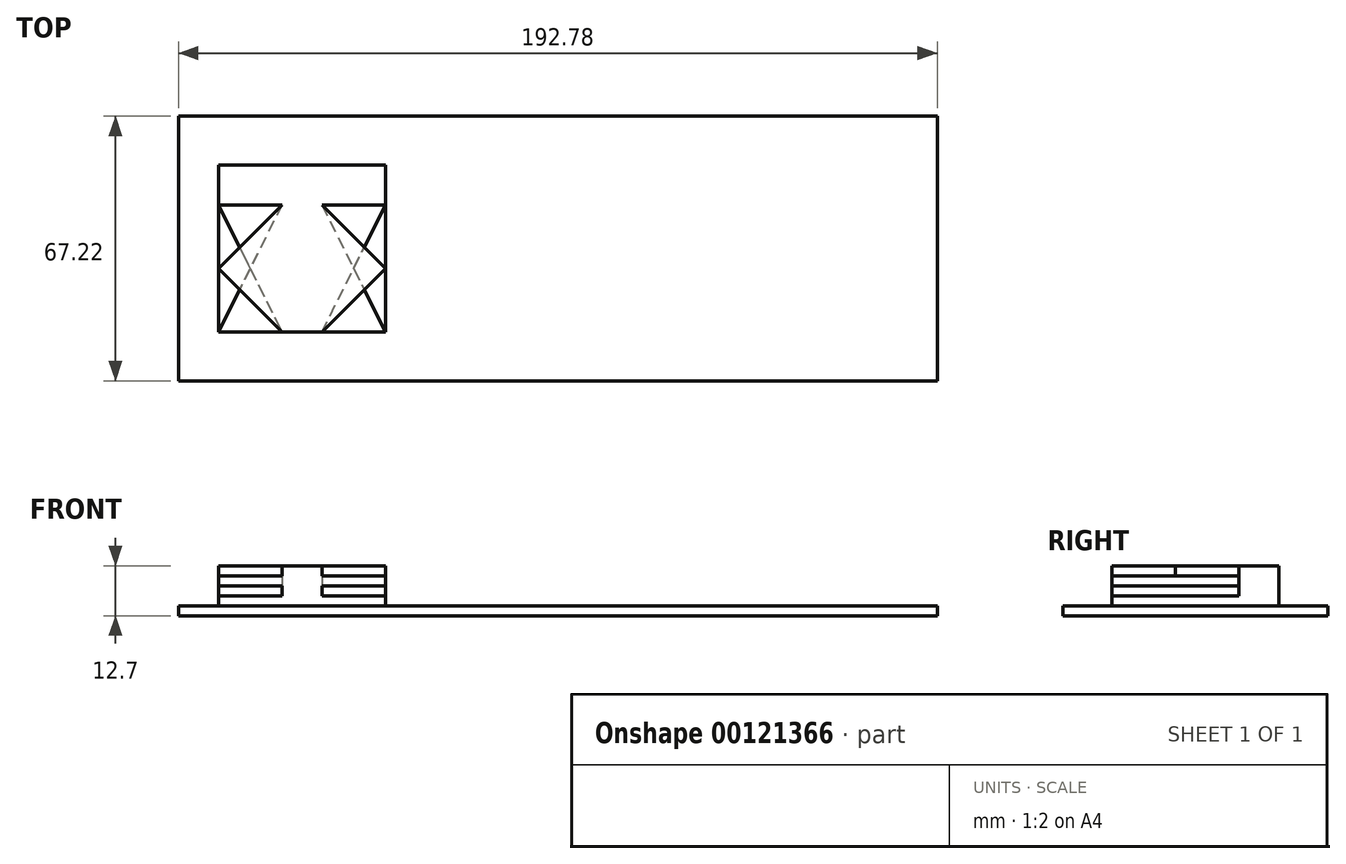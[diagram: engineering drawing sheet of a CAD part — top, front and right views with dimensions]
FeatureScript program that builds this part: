
annotation { "Feature Type Name" : "Feature", "Feature Type Description" : "" }
export const myFeature = defineFeature(function(context is Context, id is Id, definition is map)
    precondition{}
    {
        {
            var Q0;
            Q0=qCreatedBy(makeId("Top.planeOp"),FACE);
            var sketch = newSketch(context, id + "F0", { "sketchPlane" : qUnion([Q0])});
            skLineSegment(sketch, "E0", {"start": v(12479.9, 12174.65) * mm, "end": v(8845.28, 8523.8) * mm});
            skLineSegment(sketch, "E1", {"start": v(8845.28, 8523.8) * mm, "end": v(12479.9, 4895.02) * mm});
            skLineSegment(sketch, "E2", {"start": v(12479.9, 4895.02) * mm, "end": v(12479.9, 12174.65) * mm});
            skLineSegment(sketch, "E3", {"start": v(15099.98, 12172.42) * mm, "end": v(15099.98, 4895.02) * mm});
            skLineSegment(sketch, "E4", {"start": v(15099.98, 4895.02) * mm, "end": v(18732.48, 4895.02) * mm});
            skLineSegment(sketch, "E5", {"start": v(18732.48, 4895.02) * mm, "end": v(15099.98, 12172.42) * mm});
            skLineSegment(sketch, "E6", {"start": v(883.22, 12179.96) * mm, "end": v(4533.88, 12179.96) * mm});
            skLineSegment(sketch, "E7", {"start": v(4533.88, 12179.96) * mm, "end": v(4533.88, 14765.45) * mm});
            skLineSegment(sketch, "E8", {"start": v(4533.88, 14765.45) * mm, "end": v(-5353.25, 14765.45) * mm});
            skLineSegment(sketch, "E9", {"start": v(-5353.25, 14765.45) * mm, "end": v(-5353.25, 12179.96) * mm});
            skLineSegment(sketch, "E10", {"start": v(-5353.25, 12179.96) * mm, "end": v(-1702.6, 12179.96) * mm});
            skLineSegment(sketch, "E11", {"start": v(-1702.6, 12179.96) * mm, "end": v(-1702.6, 4879.79) * mm});
            skLineSegment(sketch, "E12", {"start": v(-1702.6, 4879.79) * mm, "end": v(883.22, 4879.79) * mm});
            skLineSegment(sketch, "E13", {"start": v(883.22, 4879.79) * mm, "end": v(883.22, 12179.96) * mm});
            skLineSegment(sketch, "E14", {"start": v(-18732.48, 14750.42) * mm, "end": v(-8865.64, 14750.42) * mm});
            skLineSegment(sketch, "E15", {"start": v(-8865.64, 14750.42) * mm, "end": v(-8865.64, 4894.82) * mm});
            skLineSegment(sketch, "E16", {"start": v(-8865.64, 4894.82) * mm, "end": v(-18732.48, 4894.82) * mm});
            skLineSegment(sketch, "E17", {"start": v(-18732.48, 4894.82) * mm, "end": v(-18732.48, 14750.42) * mm});
            skLineSegment(sketch, "E18.bottom", {"start": v(96.39, -33.61) * mm, "end": v(-96.39, -33.61) * mm});
            skLineSegment(sketch, "E18.top", {"start": v(96.39, 33.61) * mm, "end": v(-96.39, 33.61) * mm});
            skLineSegment(sketch, "E18.left", {"start": v(96.39, -33.61) * mm, "end": v(96.39, 33.61) * mm});
            skLineSegment(sketch, "E18.right", {"start": v(-96.39, -33.61) * mm, "end": v(-96.39, 33.61) * mm});
            skPoint(sketch, "E18.middle", {"position": v(0, 0) * mm});
            skSolve(sketch);
        }
        {
            var Q0;
            Q0=makeQuery(id+"F0.imprint","IMPRINT",FACE,{"disambiguationData":[TD([[makeQuery(id+"F0.imprint","IMPRINT",EDGE,{"derivedFrom":sQuery(id+"F0.wireOp",EDGE,"FW5R2YLv-ctxC-GVFr-Jofu-nXype2otcPYi.bottom")}),-1.0]])]});
            var Q1;
            Q1=makeQuery(id+"F0.imprint","IMPRINT",FACE,{"disambiguationData":[TD([[makeQuery(id+"F0.imprint","IMPRINT",EDGE,{"derivedFrom":sQuery(id+"F0.wireOp",EDGE,"E18.bottom")}),-1.0]])]});
            extrude(context, id + "F1", {"entities" : qUnion([Q0, Q1]), "depth" : 2.54 * mm});
        }
        {
            var Q0;
            Q0=makeQuery(id+"F1.opExtrude","CAP_FACE",FACE,{"disambiguationData":[OSD([sQuery(id+"F0.wireOp",EDGE,"E18.bottom"),sQuery(id+"F0.wireOp",EDGE,"E18.top"),sQuery(id+"F0.wireOp",EDGE,"E18.left"),sQuery(id+"F0.wireOp",EDGE,"E18.right")])],"isStart":false});
            var sketch = newSketch(context, id + "F2", { "sketchPlane" : qUnion([Q0])});
            skLineSegment(sketch, "E19.bottom", {"start": v(-43.8, -21.22) * mm, "end": v(-86.23, -21.22) * mm});
            skLineSegment(sketch, "E19.top", {"start": v(-43.8, 21.22) * mm, "end": v(-86.23, 21.22) * mm});
            skLineSegment(sketch, "E19.left", {"start": v(-43.8, -21.22) * mm, "end": v(-43.8, 21.22) * mm});
            skLineSegment(sketch, "E19.right", {"start": v(-86.23, -21.22) * mm, "end": v(-86.23, 21.22) * mm});
            skPoint(sketch, "E19.middle", {"position": v(-65.01, 0) * mm});
            skSolve(sketch);
        }
        {
            var Q0;
            Q0=makeQuery(id+"F2.imprint","IMPRINT",FACE,{"disambiguationData":[TD([[makeQuery(id+"F2.imprint","IMPRINT",EDGE,{"derivedFrom":sQuery(id+"F2.wireOp",EDGE,"E19.bottom")}),-1.0]])]});
            extrude(context, id + "F3", {"entities" : qUnion([Q0]), "depth" : 2.54 * mm});
        }
        {
            var Q0;
            Q0=makeQuery(id+"F3.opExtrude","CAP_FACE",FACE,{"disambiguationData":[OSD([sQuery(id+"F2.wireOp",EDGE,"E19.bottom"),sQuery(id+"F2.wireOp",EDGE,"E19.top"),sQuery(id+"F2.wireOp",EDGE,"E19.left"),sQuery(id+"F2.wireOp",EDGE,"E19.right")])],"isStart":false});
            var sketch = newSketch(context, id + "F4", { "sketchPlane" : qUnion([Q0])});
            skLineSegment(sketch, "E20", {"start": v(-86.23, 21.22) * mm, "end": v(-86.23, 11.06) * mm});
            skLineSegment(sketch, "E21", {"start": v(-86.23, 11.06) * mm, "end": v(-70.1, 11.06) * mm});
            skLineSegment(sketch, "E22", {"start": v(-70.1, 11.06) * mm, "end": v(-70.1, -21.22) * mm});
            skLineSegment(sketch, "E23", {"start": v(-70.1, -21.22) * mm, "end": v(-59.93, -21.22) * mm});
            skLineSegment(sketch, "E24", {"start": v(-59.93, -21.22) * mm, "end": v(-59.93, 11.06) * mm});
            skLineSegment(sketch, "E25", {"start": v(-59.93, 11.06) * mm, "end": v(-43.8, 11.06) * mm});
            skLineSegment(sketch, "E26", {"start": v(-43.8, 11.06) * mm, "end": v(-43.8, 21.22) * mm});
            skLineSegment(sketch, "E27", {"start": v(-43.8, 21.22) * mm, "end": v(-86.23, 21.22) * mm});
            skPoint(sketch, "E28", {"position": v(-65.01, -21.22) * mm});
            skSolve(sketch);
        }
        {
            var Q0;
            Q0=makeQuery(id+"F4.imprint","IMPRINT",FACE,{"disambiguationData":[TD([[makeQuery(id+"F4.imprint","IMPRINT",EDGE,{"derivedFrom":sQuery(id+"F4.wireOp",EDGE,"E20")}),-1.0]])]});
            extrude(context, id + "F5", {"entities" : qUnion([Q0]), "depth" : 7.62 * mm});
        }
        {
            var Q0;
            Q0=makeQuery(id+"F3.opExtrude","CAP_FACE",FACE,{"disambiguationData":[OSD([sQuery(id+"F2.wireOp",EDGE,"E19.bottom"),sQuery(id+"F2.wireOp",EDGE,"E19.top"),sQuery(id+"F2.wireOp",EDGE,"E19.left"),sQuery(id+"F2.wireOp",EDGE,"E19.right")])],"isStart":false});
            var sketch = newSketch(context, id + "F6", { "sketchPlane" : qUnion([Q0])});
            skPoint(sketch, "E29.0", {"position": v(-86.23, 11.06) * mm});
            skPoint(sketch, "E30.0", {"position": v(-70.1, 11.06) * mm});
            skPoint(sketch, "E31.0", {"position": v(-70.1, -21.22) * mm});
            skPoint(sketch, "E32.0", {"position": v(-59.93, -21.22) * mm});
            skPoint(sketch, "E33.0", {"position": v(-59.93, 11.06) * mm});
            skPoint(sketch, "E34.0", {"position": v(-43.8, 11.06) * mm});
            skLineSegment(sketch, "E35", {"start": v(-86.23, 11.06) * mm, "end": v(-70.1, -21.22) * mm});
            skLineSegment(sketch, "E36", {"start": v(-70.1, 11.06) * mm, "end": v(-86.23, 11.06) * mm});
            skLineSegment(sketch, "E37", {"start": v(-59.93, 11.06) * mm, "end": v(-43.8, 11.06) * mm});
            skLineSegment(sketch, "E38", {"start": v(-59.93, -21.22) * mm, "end": v(-59.93, 11.06) * mm});
            skLineSegment(sketch, "E39", {"start": v(-59.93, -21.22) * mm, "end": v(-43.8, 11.06) * mm});
            skLineSegment(sketch, "E40", {"start": v(-70.1, 11.06) * mm, "end": v(-70.1, -21.22) * mm});
            skSolve(sketch);
        }
        {
            var Q0;
            Q0=makeQuery(id+"F6.imprint","IMPRINT",FACE,{"disambiguationData":[TD([[makeQuery(id+"F6.imprint","IMPRINT",EDGE,{"derivedFrom":sQuery(id+"F6.wireOp",EDGE,"E35")}),1.0]])]});
            var Q1;
            Q1=makeQuery(id+"F6.imprint","IMPRINT",FACE,{"disambiguationData":[TD([[makeQuery(id+"F6.imprint","IMPRINT",EDGE,{"derivedFrom":sQuery(id+"F6.wireOp",EDGE,"E37")}),-1.0]])]});
            extrude(context, id + "F7", {"entities" : qUnion([Q0, Q1]), "operationType" : NewBodyOperationType.ADD, "depth" : 2.54 * mm});
        }
        {
            var Q0;
            Q0=makeQuery(id+"F7.opExtrude","CAP_FACE",FACE,{"disambiguationData":[OSD([sQuery(id+"F6.wireOp",EDGE,"E35"),sQuery(id+"F6.wireOp",EDGE,"E36"),sQuery(id+"F6.wireOp",EDGE,"E40")])],"isStart":false});
            var sketch = newSketch(context, id + "F8", { "sketchPlane" : qUnion([Q0])});
            skLineSegment(sketch, "E41.0", {"start": v(-70.1, -21.22) * mm, "end": v(-86.23, -21.22) * mm});
            skLineSegment(sketch, "E42.0", {"start": v(-70.1, 11.06) * mm, "end": v(-70.1, -21.22) * mm});
            skLineSegment(sketch, "E43.0", {"start": v(-59.93, -21.22) * mm, "end": v(-59.93, 11.06) * mm});
            skLineSegment(sketch, "E44.0", {"start": v(-43.8, -21.22) * mm, "end": v(-59.93, -21.22) * mm});
            skLineSegment(sketch, "E45", {"start": v(-70.1, 11.06) * mm, "end": v(-86.23, -21.22) * mm});
            skLineSegment(sketch, "E46", {"start": v(-59.93, 11.06) * mm, "end": v(-43.8, -21.22) * mm});
            skSolve(sketch);
        }
        {
            var Q0;
            Q0 = qSketchRegion(id + "F8", true);
            extrude(context, id + "F9", {"entities" : qUnion([Q0]), "operationType" : NewBodyOperationType.ADD, "depth" : 2.54 * mm});
        }
        {
            var Q0;
            Q0=makeQuery(id+"F9.opExtrude","CAP_FACE",FACE,{"disambiguationData":[OSD([sQuery(id+"F8.wireOp",EDGE,"E41.0"),sQuery(id+"F8.wireOp",EDGE,"E42.0"),sQuery(id+"F8.wireOp",EDGE,"E45")])],"isStart":false});
            var sketch = newSketch(context, id + "F10", { "sketchPlane" : qUnion([Q0])});
            skLineSegment(sketch, "E47.0", {"start": v(-70.1, 11.06) * mm, "end": v(-70.1, -21.22) * mm});
            skLineSegment(sketch, "E48.0", {"start": v(-59.93, -21.22) * mm, "end": v(-59.93, 11.06) * mm});
            skLineSegment(sketch, "E49.0", {"start": v(-86.23, -21.22) * mm, "end": v(-86.23, 11.06) * mm, "construction": true});
            skLineSegment(sketch, "E50.0", {"start": v(-43.8, -21.22) * mm, "end": v(-43.8, 11.06) * mm, "construction": true});
            skLineSegment(sketch, "E51", {"start": v(-86.23, -5.08) * mm, "end": v(-70.1, -21.22) * mm});
            skLineSegment(sketch, "E52", {"start": v(-86.23, -5.08) * mm, "end": v(-70.1, 11.06) * mm});
            skLineSegment(sketch, "E53", {"start": v(-59.93, 11.06) * mm, "end": v(-43.8, -5.08) * mm});
            skLineSegment(sketch, "E54", {"start": v(-43.8, -5.08) * mm, "end": v(-59.93, -21.22) * mm});
            skSolve(sketch);
        }
        {
            var Q0;
            Q0 = qSketchRegion(id + "F10", true);
            var Q1;
            Q1 = qConstructionFilter(qBodyType(qCreatedBy(id + "F10" ,EDGE), BodyType.WIRE), ConstructionObject.NO);
            extrude(context, id + "F11", {"entities" : qUnion([Q0]), "operationType" : NewBodyOperationType.ADD, "surfaceEntities" : qUnion([Q1]), "depth" : 2.54 * mm});
        }
    });
